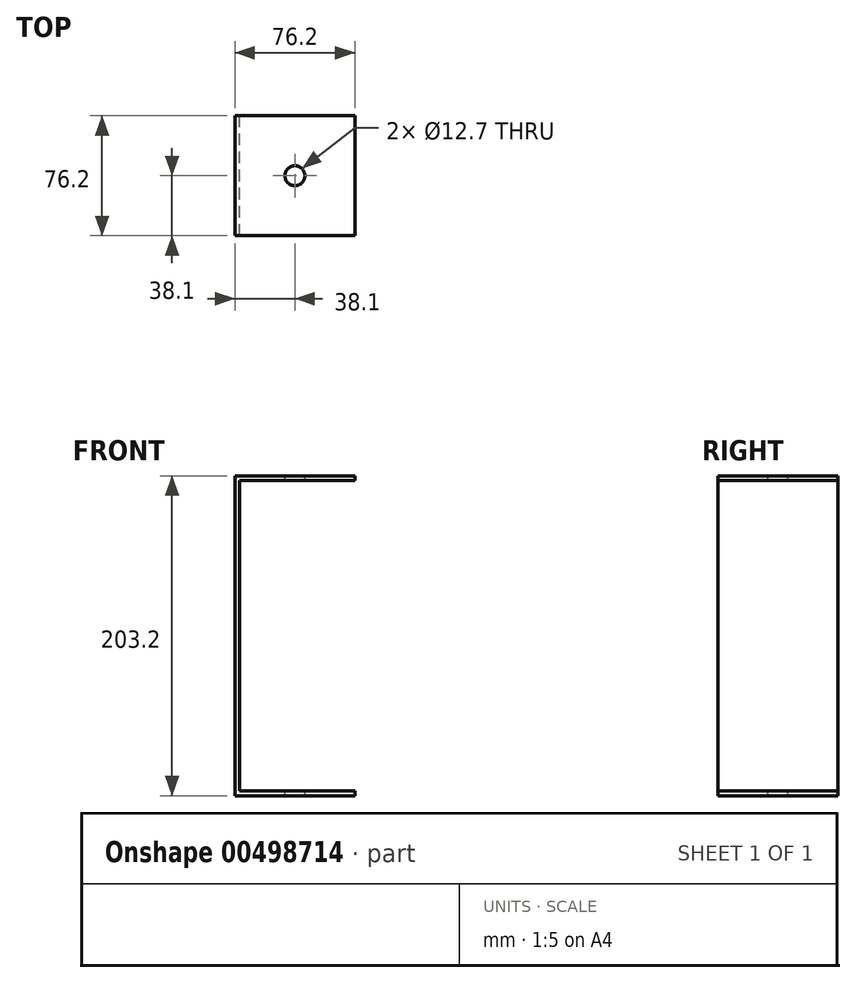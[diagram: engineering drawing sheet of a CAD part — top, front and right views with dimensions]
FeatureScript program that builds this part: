
annotation { "Feature Type Name" : "Feature", "Feature Type Description" : "" }
export const myFeature = defineFeature(function(context is Context, id is Id, definition is map)
    precondition{}
    {
        {
            var Q0;
            Q0=qCreatedBy(makeId("Front.planeOp"),FACE);
            var sketch = newSketch(context, id + "F0", { "sketchPlane" : qUnion([Q0])});
            skLineSegment(sketch, "E0", {"start": v(0, 0) * mm, "end": v(0, 101.6) * mm});
            skLineSegment(sketch, "E1", {"start": v(0, 101.6) * mm, "end": v(76.2, 101.6) * mm});
            skLineSegment(sketch, "E2.0", {"start": v(3, 98.6) * mm, "end": v(76.2, 98.6) * mm});
            skLineSegment(sketch, "E2.1", {"start": v(3, 0) * mm, "end": v(3, 98.6) * mm});
            skLineSegment(sketch, "E3", {"start": v(76.2, 101.6) * mm, "end": v(76.2, 98.6) * mm});
            skLineSegment(sketch, "E4", {"start": v(0, 0) * mm, "end": v(60.86, 0) * mm, "construction": true});
            skLineSegment(sketch, "E5.MirrorCS", {"start": v(0, -101.6) * mm, "end": v(76.2, -101.6) * mm});
            skLineSegment(sketch, "E6.MirrorCS", {"start": v(3, -98.6) * mm, "end": v(76.2, -98.6) * mm});
            skLineSegment(sketch, "E7.MirrorCS", {"start": v(76.2, -101.6) * mm, "end": v(76.2, -98.6) * mm});
            skLineSegment(sketch, "E8.MirrorCS", {"start": v(0, 0) * mm, "end": v(0, -101.6) * mm});
            skLineSegment(sketch, "E9.MirrorCS", {"start": v(3, 0) * mm, "end": v(3, -98.6) * mm});
            skSolve(sketch);
        }
        {
            var Q0;
            Q0=makeQuery(id+"F0.imprint","IMPRINT",FACE,{"disambiguationData":[TD([[makeQuery(id+"F0.imprint","IMPRINT",EDGE,{"derivedFrom":sQuery(id+"F0.wireOp",EDGE,"E0")}),-1.0]])]});
            extrude(context, id + "F1", {"entities" : qUnion([Q0]), "endBound" : BoundingType.SYMMETRIC, "depth" : 76.2 * mm, "hasSecondDirection" : true, "secondDirectionOppositeDirection" : true, "secondDirectionDepth" : 25.4 * mm});
        }
        {
            var Q0;
            Q0=makeQuery(id+"F1.opExtrude","SWEPT_FACE",FACE,{"disambiguationData":[OSD([sQuery(id+"F0.wireOp",EDGE,"E1")])]});
            var sketch = newSketch(context, id + "F2", { "sketchPlane" : qUnion([Q0])});
            skCircle(sketch, "E10", {"center": v(38.1, 0) * mm, "radius": 6.35 * mm});
            skSolve(sketch);
        }
        {
            var Q0;
            Q0=makeQuery(id+"F2.imprint","IMPRINT",FACE,{"disambiguationData":[TD([[makeQuery(id+"F2.imprint","IMPRINT",EDGE,{"derivedFrom":sQuery(id+"F2.wireOp",EDGE,"E10")}),1.0]])]});
            extrude(context, id + "F3", {"entities" : qUnion([Q0]), "operationType" : NewBodyOperationType.REMOVE, "oppositeDirection" : true, "depth" : 286.87 * mm});
        }
    });
